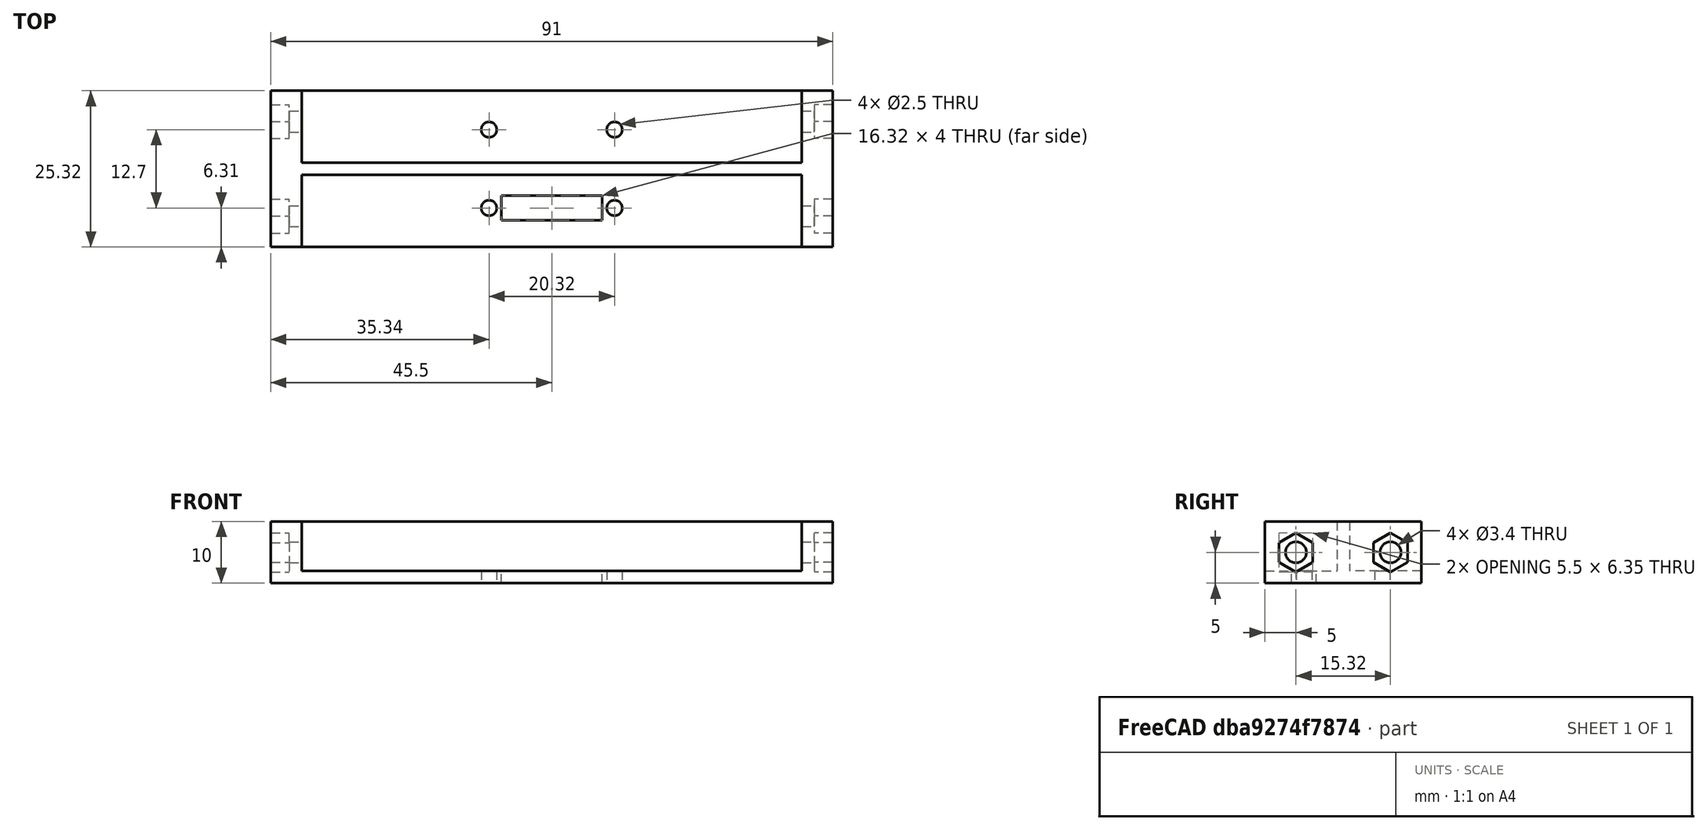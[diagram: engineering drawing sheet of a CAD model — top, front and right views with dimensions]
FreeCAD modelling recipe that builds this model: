
FCSTD DOCUMENT  (FreeCAD 0.21R33668 +26 (Git))
Label: Support_MLX
License: All rights reserved
LicenseURL: http://en.wikipedia.org/wiki/All_rights_reserved
objects: Sketcher::SketchObject×7, PartDesign::Pocket×4, App::DocumentObjectGroup×3, PartDesign::CoordinateSystem×3, PartDesign::Hole×2, Spreadsheet::Sheet×1, App::FeaturePython×1, PartDesign::Pad×1, PartDesign::Body×1, App::Part×1, Mesh::Feature×1
note: 25 computed .brp shape members not serialized (recipe doc carries the construction recipe); baked Part::Feature solids carry a one-line shape summary decoded from their .brp
EXTERNAL_REF file=MLX90640.FCStd obj=Spreadsheet

FEATURE [Spreadsheet::Sheet] Spreadsheet
  cells = B2='MLX; B3='mlx_Hdist; C3(mlx_Hdist)==<<MLX90640>>#<<Spreadsheet>>.holes_Hdist; E3='walls_thickness; F3(walls_thickness)==2 mm; H3='nut_wall_thickness; I3(nut_wall_thickness)==5 mm; B4='mlx_Vdist; C4(mlx_Vdist)==<<MLX90640>>#<<Spreadsheet>>.holes_Vdist; E4='extra_space; F4(extra_space)==5 mm; H4='nut_depth; I4(nut_depth)==3 mm; B5='mlx_screw_radius; C5(mlx_screw_radius)==<<MLX90640>>#<<Spreadsheet>>.holes_rad; E5='carrier_width; F5(carrier_width)==10 mm; H5='nut_edge; I5(nut_edge)==5.5 mm; E6='carrier_height; F6(carrier_height)==mlx_Hdist + extra_space; B7='main_case_width; C7(main_case_width)==95 mm; E7='carrier_length; F7(carrier_length)==main_case_width - walls_thickness * 2; E8='screw_radius; F8(screw_radius)==1.5 mm
FEATURE [App::DocumentObjectGroup] Parts
FEATURE [PartDesign::CoordinateSystem] LCS_Origin
  AttacherType = Attacher::AttachEngine3D
  MapMode = 2
  Support = -> [X_Axis]
FEATURE [App::DocumentObjectGroup] Constraints
FEATURE [App::FeaturePython] Variables  # WARN: FeaturePython — macro-defined, semantics opaque (R4)
  Type = App::PropertyContainer
FEATURE [App::DocumentObjectGroup] Configurations
FEATURE [Sketcher::SketchObject] Sketch
  FullyConstrained = true
  MapMode = 5
  Support = -> [XY_Plane001]
  expr: Constraints[7] = <<Spreadsheet>>.carrier_length
  expr: Constraints[8] = <<Spreadsheet>>.carrier_height
  sketch-geometry (4):
    g0: LineSegment StartX=-45.5 StartY=12.66 StartZ=0 EndX=45.5 EndY=12.66 EndZ=0
    g1: LineSegment StartX=45.5 StartY=12.66 StartZ=0 EndX=45.5 EndY=-12.66 EndZ=0
    g2: LineSegment StartX=45.5 StartY=-12.66 StartZ=0 EndX=-45.5 EndY=-12.66 EndZ=0
    g3: LineSegment StartX=-45.5 StartY=-12.66 StartZ=0 EndX=-45.5 EndY=12.66 EndZ=0
  constraints (9):
    c: Coincident(g0,g1)
    c: Coincident(g1,g2)
    c: Coincident(g2,g3)
    c: Coincident(g3,g0)
    c: Symmetric(g0,g0,g-2)
    c: Symmetric(g0,g2,g-1)
    c: Symmetric(g0,g1,g-1)
    c: DistanceX(g0,g0) = 91
    c: DistanceY(g3,g3) = 25.32
FEATURE [PartDesign::Pad] Pad
  Direction = (0,0,1)
  Length = 10
  Length2 = 10
  Profile = -> Sketch
  ReferenceAxis = -> Sketch [N_Axis]
  Type = 0
  expr: Length = <<Spreadsheet>>.carrier_width
FEATURE [Sketcher::SketchObject] Sketch001
  ExternalGeometry = -> [Pad]
  FullyConstrained = true
  MapMode = 5
  Placement = pos=(0,0,10) rot=(0,0,1;0rad)
  Support = -> [Pad]
  expr: Constraints[19] = <<Spreadsheet>>.nut_wall_thickness
  expr: Constraints[20] = <<Spreadsheet>>.nut_wall_thickness
  expr: Constraints[21] = <<Spreadsheet>>.walls_thickness
  sketch-geometry (8):
    g0: LineSegment StartX=-40.5 StartY=12.66 StartZ=0 EndX=40.5 EndY=12.66 EndZ=0
    g1: LineSegment StartX=40.5 StartY=12.66 StartZ=0 EndX=40.5 EndY=1 EndZ=0
    g2: LineSegment StartX=40.5 StartY=1 StartZ=0 EndX=-40.5 EndY=1 EndZ=0
    g3: LineSegment StartX=-40.5 StartY=1 StartZ=0 EndX=-40.5 EndY=12.66 EndZ=0
    g4: LineSegment StartX=-40.5 StartY=-12.66 StartZ=0 EndX=40.5 EndY=-12.66 EndZ=0
    g5: LineSegment StartX=40.5 StartY=-12.66 StartZ=0 EndX=40.5 EndY=-1 EndZ=0
    g6: LineSegment StartX=40.5 StartY=-1 StartZ=0 EndX=-40.5 EndY=-1 EndZ=0
    g7: LineSegment StartX=-40.5 StartY=-1 StartZ=0 EndX=-40.5 EndY=-12.66 EndZ=0
  constraints (22):
    c: Coincident(g0,g1)
    c: Coincident(g1,g2)
    c: Coincident(g2,g3)
    c: Coincident(g3,g0)
    c: Horizontal(g0)
    c: Horizontal(g2)
    c: Vertical(g1)
    c: Vertical(g3)
    c: PointOnObject(g0,g-3)
    c: Coincident(g4,g5)
    c: Coincident(g5,g6)
    c: Coincident(g6,g7)
    c: Coincident(g7,g4)
    c: Horizontal(g4)
    c: Vertical(g5)
    c: Vertical(g7)
    c: PointOnObject(g4,g-5)
    c: Symmetric(g2,g6,g-1)
    c: Symmetric(g1,g5,g-1)
    c: DistanceX(g-4,g0) = 5
    c: DistanceX(g0,g-6) = 5
    c: DistanceY(g6,g2) = 2
FEATURE [PartDesign::Pocket] Pocket
  BaseFeature = -> Pad
  Direction = (0,0,-1)
  Length = 8
  Length2 = 5
  Profile = -> Sketch001
  ReferenceAxis = -> Sketch001 [N_Axis]
  Type = 0
  expr: Length = <<Spreadsheet>>.carrier_width - <<Spreadsheet>>.walls_thickness
FEATURE [Sketcher::SketchObject] Sketch004
  FullyConstrained = true
  MapMode = 5
  Placement = pos=(0,0,2) rot=(0,0,1;0rad)
  expr: Constraints[3] = <<Spreadsheet>>.mlx_Hdist
  expr: Constraints[4] = <<Spreadsheet>>.mlx_Vdist
  expr: Constraints[5] = <<Spreadsheet>>.mlx_screw_radius
  expr: Constraints[6] = <<Spreadsheet>>.mlx_screw_radius
  expr: Constraints[7] = <<Spreadsheet>>.mlx_screw_radius
  expr: Constraints[8] = <<Spreadsheet>>.mlx_screw_radius
  sketch-geometry (4):
    g0: Circle CenterX=10.16 CenterY=6.35 CenterZ=0 NormalX=0 NormalY=0 NormalZ=1 AngleXU=0 Radius=1.27
    g1: Circle CenterX=-10.16 CenterY=6.35 CenterZ=0 NormalX=0 NormalY=0 NormalZ=1 AngleXU=0 Radius=1.27
    g2: Circle CenterX=-10.16 CenterY=-6.35 CenterZ=0 NormalX=0 NormalY=0 NormalZ=1 AngleXU=0 Radius=1.27
    g3: Circle CenterX=10.16 CenterY=-6.35 CenterZ=0 NormalX=0 NormalY=0 NormalZ=1 AngleXU=0 Radius=1.27
  constraints (9):
    c: Symmetric(g1,g0,g-2)
    c: Symmetric(g2,g3,g-2)
    c: Symmetric(g1,g3,g-1)
    c: DistanceX(g1,g0) = 20.32
    c: DistanceY(g2,g1) = 12.7
    c: Radius(g1) = 1.27
    c: Radius(g0) = 1.27
    c: Radius(g2) = 1.27
    c: Radius(g3) = 1.27
FEATURE [PartDesign::Hole] Hole002
  BaseFeature = -> Pocket
  CustomThreadClearance = 0
  Depth = 2
  DepthType = 0
  Diameter = 2.5
  DrillForDepth = false
  DrillPoint = 1
  DrillPointAngle = 118
  HoleCutCountersinkAngle = 90
  HoleCutCustomValues = false
  HoleCutDepth = 0
  HoleCutDiameter = 6.1
  HoleCutType = 0
  ModelThread = false
  Profile = -> Sketch004
  Tapered = false
  TaperedAngle = 90
  ThreadClass = 0
  ThreadDepth = 2
  ThreadDepthType = 0
  ThreadDirection = 0
  ThreadFit = 0
  ThreadSize = 9
  ThreadType = 1
  Threaded = true
  UseCustomThreadClearance = false
  expr: Depth = <<Spreadsheet>>.walls_thickness
FEATURE [Sketcher::SketchObject] Sketch005
  ExternalGeometry = -> [Hole002]
  FullyConstrained = true
  MapMode = 5
  Placement = pos=(-45.5,0,0) rot=(0.57735,-0.57735,-0.57735;2.0944rad)
  Support = -> [Hole002]
  expr: Constraints[0] = <<Spreadsheet>>.carrier_width / 2
  expr: Constraints[1] = <<Spreadsheet>>.carrier_width / 2
  expr: Constraints[2] = <<Spreadsheet>>.carrier_width / 2
  expr: Constraints[3] = <<Spreadsheet>>.carrier_width / 2
  expr: Constraints[4] = <<Spreadsheet>>.screw_radius
  expr: Constraints[5] = <<Spreadsheet>>.screw_radius
  sketch-geometry (2):
    g0: Circle CenterX=-7.66 CenterY=5 CenterZ=0 NormalX=0 NormalY=0 NormalZ=1 AngleXU=0 Radius=1.5
    g1: Circle CenterX=7.66 CenterY=5 CenterZ=0 NormalX=0 NormalY=0 NormalZ=1 AngleXU=0 Radius=1.5
  constraints (6):
    c: DistanceX(g-4,g0) = 5
    c: DistanceX(g1,g-6) = 5
    c: DistanceY(g0,g-4) = 5
    c: DistanceY(g1,g-6) = 5
    c: Radius(g0) = 1.5
    c: Radius(g1) = 1.5
FEATURE [PartDesign::Hole] Hole
  BaseFeature = -> Hole002
  CustomThreadClearance = 0
  Depth = 191.869
  DepthType = 1
  Diameter = 3.4
  DrillForDepth = false
  DrillPoint = 1
  DrillPointAngle = 118
  HoleCutCountersinkAngle = 90
  HoleCutCustomValues = false
  HoleCutDepth = 0
  HoleCutDiameter = 6.1
  HoleCutType = 0
  ModelThread = false
  Profile = -> Sketch005
  Tapered = false
  TaperedAngle = 90
  ThreadClass = 0
  ThreadDepth = 191.869
  ThreadDepthType = 0
  ThreadDirection = 0
  ThreadFit = 0
  ThreadSize = 9
  ThreadType = 1
  Threaded = false
  UseCustomThreadClearance = false
FEATURE [PartDesign::CoordinateSystem] LCS_MLX
  AttacherType = Attacher::AttachEngine3D
  MapMode = 11
  Placement = pos=(-10.16,-6.35,2.2e-15) rot=(0,0,1;1.5708rad)
  Support = -> [Hole]
FEATURE [Sketcher::SketchObject] Sketch006
  ExternalGeometry = -> [Hole]
  FullyConstrained = true
  MapMode = 5
  Placement = pos=(0,0,0) rot=(1,0,0;3.14159rad)
  Support = -> [Hole]
  sketch-geometry (5):
    g0: LineSegment StartX=-8.16 StartY=8.35 StartZ=0 EndX=8.16 EndY=8.35 EndZ=0
    g1: LineSegment StartX=8.16 StartY=8.35 StartZ=0 EndX=8.16 EndY=4.35 EndZ=0
    g2: LineSegment StartX=8.16 StartY=4.35 StartZ=0 EndX=-8.16 EndY=4.35 EndZ=0
    g3: LineSegment StartX=-8.16 StartY=4.35 StartZ=0 EndX=-8.16 EndY=8.35 EndZ=0
    g4: GeomPoint X=3e-16 Y=6.35 Z=0
  constraints (11):
    c: Coincident(g0,g1)
    c: Coincident(g1,g2)
    c: Coincident(g2,g3)
    c: Coincident(g3,g0)
    c: Horizontal(g2)
    c: Vertical(g3)
    c: Symmetric(g0,g0,g-2)
    c: DistanceX(g-3,g0) = 2
    c: Symmetric(g-3,g-4,g4)
    c: Symmetric(g0,g1,g4)
    c: DistanceY(g3,g3) = 4
FEATURE [PartDesign::Pocket] Pocket001
  BaseFeature = -> Hole
  Direction = (0,0,1)
  Length = 2
  Length2 = 5
  Profile = -> Sketch006
  ReferenceAxis = -> Sketch006 [N_Axis]
  Type = 0
  expr: Length = <<Spreadsheet>>.walls_thickness
FEATURE [PartDesign::CoordinateSystem] LCS_carrier
  AttacherType = Attacher::AttachEngine3D
  MapMode = 11
  Placement = pos=(-45.5,-7.66,5) rot=(0.57735,0.57735,-0.57735;4.18879rad)
  Support = -> [Pocket001]
FEATURE [Sketcher::SketchObject] Sketch007
  ExternalGeometry = -> [Pocket001]
  FullyConstrained = true
  MapMode = 5
  Placement = pos=(45.5,-1.27e-14,0) rot=(0.57735,0.57735,0.57735;2.0944rad)
  Support = -> [Pocket001]
  expr: Constraints[38] = Spreadsheet.nut_edge
  expr: Constraints[39] = Spreadsheet.nut_edge
  sketch-geometry (14):
    g0: LineSegment StartX=-4.91 StartY=6.58771 StartZ=0 EndX=-7.66 EndY=8.17543 EndZ=0
    g1: LineSegment StartX=-7.66 StartY=8.17543 StartZ=0 EndX=-10.41 EndY=6.58771 EndZ=0
    g2: LineSegment StartX=-10.41 StartY=6.58771 StartZ=0 EndX=-10.41 EndY=3.41229 EndZ=0
    g3: LineSegment StartX=-10.41 StartY=3.41229 StartZ=0 EndX=-7.66 EndY=1.82457 EndZ=0
    g4: LineSegment StartX=-7.66 StartY=1.82457 StartZ=0 EndX=-4.91 EndY=3.41229 EndZ=0
    g5: LineSegment StartX=-4.91 StartY=3.41229 StartZ=0 EndX=-4.91 EndY=6.58771 EndZ=0
    g6: Circle CenterX=-7.66 CenterY=5 CenterZ=0 NormalX=0 NormalY=0 NormalZ=1 AngleXU=0 Radius=3.17543
    g7: LineSegment StartX=10.41 StartY=6.58771 StartZ=0 EndX=7.66 EndY=8.17543 EndZ=0
    g8: LineSegment StartX=7.66 StartY=8.17543 StartZ=0 EndX=4.91 EndY=6.58771 EndZ=0
    g9: LineSegment StartX=4.91 StartY=6.58771 StartZ=0 EndX=4.91 EndY=3.41229 EndZ=0
    g10: LineSegment StartX=4.91 StartY=3.41229 StartZ=0 EndX=7.66 EndY=1.82457 EndZ=0
    g11: LineSegment StartX=7.66 StartY=1.82457 StartZ=0 EndX=10.41 EndY=3.41229 EndZ=0
    g12: LineSegment StartX=10.41 StartY=3.41229 StartZ=0 EndX=10.41 EndY=6.58771 EndZ=0
    g13: Circle CenterX=7.66 CenterY=5 CenterZ=0 NormalX=0 NormalY=0 NormalZ=1 AngleXU=0 Radius=3.17543
  constraints (32):
    c: Coincident(g1,g2)
    c: Coincident(g2,g3)
    c: Coincident(g3,g4)
    c: Coincident(g4,g5)
    c: Coincident(g5,g0)
    c: Equal(g0, g1-g5) x5
    c: PointOnObject(g0,g6)
    c: PointOnObject(g1,g6)
    c: PointOnObject(g2,g6)
    c: PointOnObject(g3,g6)
    c: PointOnObject(g4,g6)
    c: PointOnObject(g5,g6)
    c: Coincident(g6,g-3)
    c: Coincident(g7,g8)
    c: Coincident(g8,g9)
    c: Coincident(g9,g10)
    c: Coincident(g10,g11)
    c: Coincident(g11,g12)
    c: Coincident(g12,g7)
    c: Equal(g7, g8-g12) x5
    c: PointOnObject(g7,g13)
    c: PointOnObject(g8,g13)
    c: PointOnObject(g9,g13)
    c: PointOnObject(g10,g13)
    c: PointOnObject(g11,g13)
    c: PointOnObject(g12,g13)
    c: Coincident(g13,g-4)
    c: Vertical(g5)
    c: Vertical(g12)
    c: Coincident(g1,g0)
    c: DistanceX(g2,g4) = 5.5
    c: DistanceX(g9,g11) = 5.5
FEATURE [PartDesign::Pocket] Pocket002
  BaseFeature = -> Pocket001
  Direction = (-1,1e-16,1e-16)
  Length = 3
  Length2 = 5
  Profile = -> Sketch007
  ReferenceAxis = -> Sketch007 [N_Axis]
  Type = 0
  expr: Length = Spreadsheet.nut_depth
FEATURE [Sketcher::SketchObject] Sketch008
  ExternalGeometry = -> [Pocket002]
  FullyConstrained = true
  MapMode = 5
  Placement = pos=(-45.5,0,0) rot=(0.57735,-0.57735,-0.57735;2.0944rad)
  Support = -> [Pocket002]
  expr: Constraints[38] = Spreadsheet.nut_edge
  expr: Constraints[39] = Spreadsheet.nut_edge
  sketch-geometry (14):
    g0: LineSegment StartX=-4.91 StartY=6.58771 StartZ=0 EndX=-7.66 EndY=8.17543 EndZ=0
    g1: LineSegment StartX=-7.66 StartY=8.17543 StartZ=0 EndX=-10.41 EndY=6.58771 EndZ=0
    g2: LineSegment StartX=-10.41 StartY=6.58771 StartZ=0 EndX=-10.41 EndY=3.41229 EndZ=0
    g3: LineSegment StartX=-10.41 StartY=3.41229 StartZ=0 EndX=-7.66 EndY=1.82457 EndZ=0
    g4: LineSegment StartX=-7.66 StartY=1.82457 StartZ=0 EndX=-4.91 EndY=3.41229 EndZ=0
    g5: LineSegment StartX=-4.91 StartY=3.41229 StartZ=0 EndX=-4.91 EndY=6.58771 EndZ=0
    g6: Circle CenterX=-7.66 CenterY=5 CenterZ=0 NormalX=0 NormalY=0 NormalZ=1 AngleXU=0 Radius=3.17543
    g7: LineSegment StartX=10.41 StartY=6.58771 StartZ=0 EndX=7.66 EndY=8.17543 EndZ=0
    g8: LineSegment StartX=7.66 StartY=8.17543 StartZ=0 EndX=4.91 EndY=6.58771 EndZ=0
    g9: LineSegment StartX=4.91 StartY=6.58771 StartZ=0 EndX=4.91 EndY=3.41229 EndZ=0
    g10: LineSegment StartX=4.91 StartY=3.41229 StartZ=0 EndX=7.66 EndY=1.82457 EndZ=0
    g11: LineSegment StartX=7.66 StartY=1.82457 StartZ=0 EndX=10.41 EndY=3.41229 EndZ=0
    g12: LineSegment StartX=10.41 StartY=3.41229 StartZ=0 EndX=10.41 EndY=6.58771 EndZ=0
    g13: Circle CenterX=7.66 CenterY=5 CenterZ=0 NormalX=0 NormalY=0 NormalZ=1 AngleXU=0 Radius=3.17543
  constraints (32):
    c: Coincident(g0,g1)
    c: Coincident(g1,g2)
    c: Coincident(g2,g3)
    c: Coincident(g3,g4)
    c: Coincident(g4,g5)
    c: Coincident(g5,g0)
    c: Equal(g0, g1-g5) x5
    c: PointOnObject(g0,g6)
    c: PointOnObject(g1,g6)
    c: PointOnObject(g2,g6)
    c: PointOnObject(g3,g6)
    c: PointOnObject(g4,g6)
    c: PointOnObject(g5,g6)
    c: Coincident(g6,g-3)
    c: Coincident(g7,g8)
    c: Coincident(g8,g9)
    c: Coincident(g9,g10)
    c: Coincident(g10,g11)
    c: Coincident(g11,g12)
    c: Coincident(g12,g7)
    c: Equal(g7, g8-g12) x5
    c: PointOnObject(g7,g13)
    c: PointOnObject(g8,g13)
    c: PointOnObject(g9,g13)
    c: PointOnObject(g10,g13)
    c: PointOnObject(g11,g13)
    c: PointOnObject(g12,g13)
    c: Coincident(g13,g-4)
    c: Vertical(g5)
    c: Vertical(g12)
    c: DistanceX(g2,g4) = 5.5
    c: DistanceX(g9,g11) = 5.5
FEATURE [PartDesign::Pocket] Pocket003
  BaseFeature = -> Pocket002
  Direction = (1,0,0)
  Length = 3
  Length2 = 5
  Profile = -> Sketch008
  ReferenceAxis = -> Sketch008 [N_Axis]
  Type = 0
  expr: Length = Spreadsheet.nut_depth
FEATURE [PartDesign::Body] Body
  Group = -> [Sketch,Pad,Sketch001,Pocket,Sketch004,Hole002,Sketch005,Hole,Sketch006,Pocket001,Sketch007,Pocket002,Sketch008,Pocket003]
  Origin = -> Origin001
  Tip = -> Pocket003
FEATURE [App::Part] Model
  AssemblyType = Part::Link
  Group = -> [LCS_Origin,Constraints,Variables,Configurations,Body,LCS_carrier,LCS_MLX]
  Origin = -> Origin
  Type = Assembly
FEATURE [Mesh::Feature] Mesh  label="Body (Meshed)"
